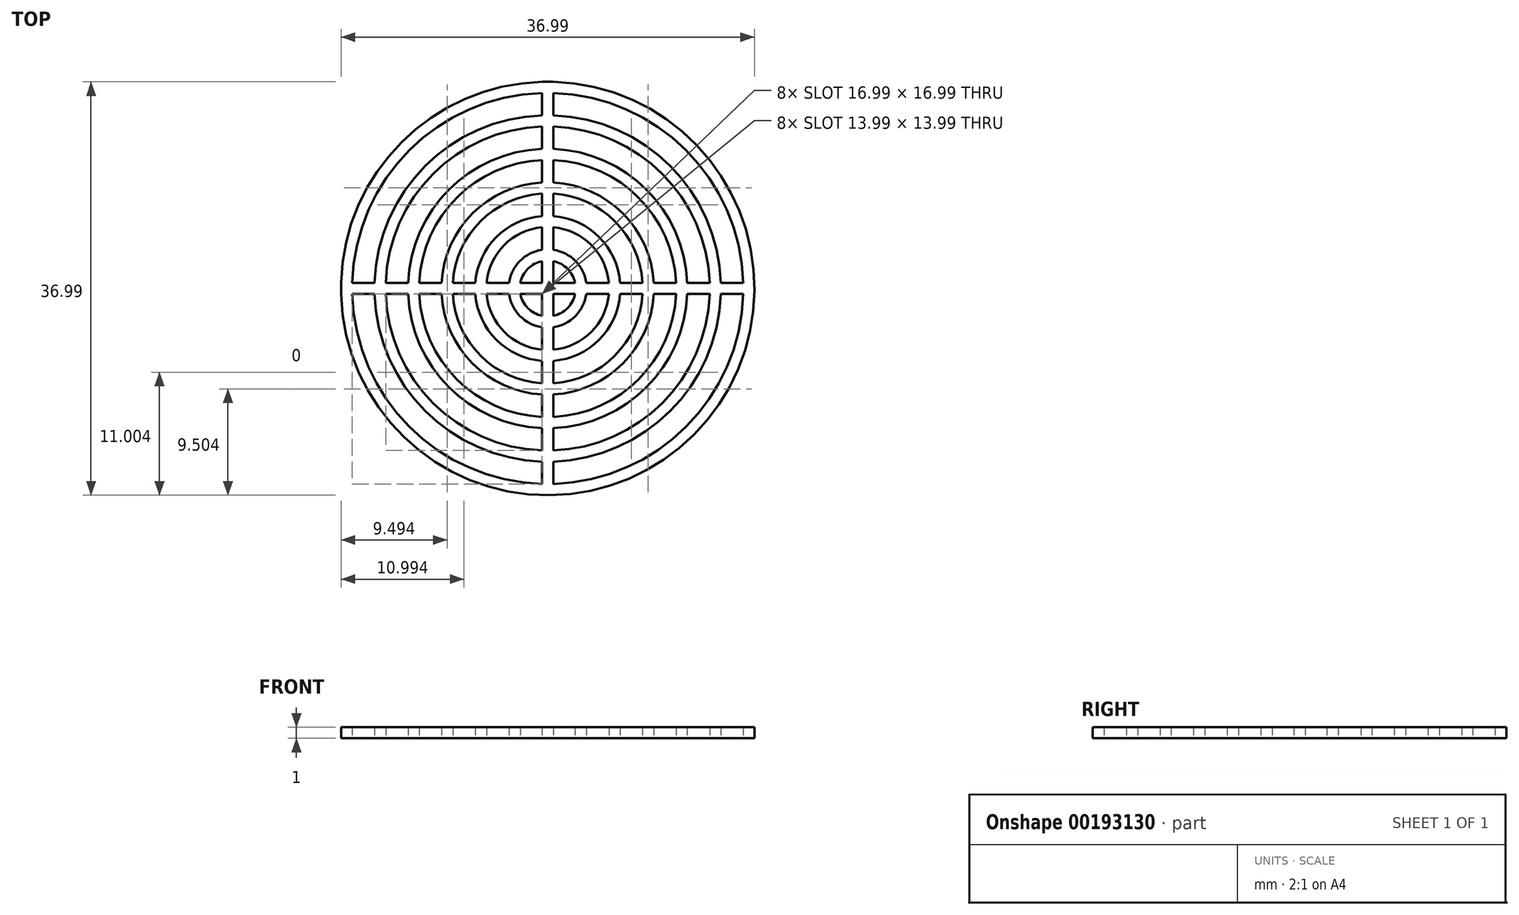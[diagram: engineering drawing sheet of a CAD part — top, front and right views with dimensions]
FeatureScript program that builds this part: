
annotation { "Feature Type Name" : "Feature", "Feature Type Description" : "" }
export const myFeature = defineFeature(function(context is Context, id is Id, definition is map)
    precondition{}
    {
        {
            var Q0;
            Q0=qCreatedBy(makeId("Top.planeOp"),FACE);
            var sketch = newSketch(context, id + "F0", { "sketchPlane" : qUnion([Q0])});
            skArc(sketch, "E0", {"start": v(-2.45, -0.5) * mm, "mid": v(-1.77, -1.77) * mm, "end": v(-0.5, -2.45) * mm});
            skArc(sketch, "E1", {"start": v(-3.46, -0.5) * mm, "mid": v(-2.47, -2.47) * mm, "end": v(-0.5, -3.46) * mm});
            skArc(sketch, "E2", {"start": v(-5.48, -0.5) * mm, "mid": v(-3.89, -3.89) * mm, "end": v(-0.5, -5.48) * mm});
            skArc(sketch, "E3", {"start": v(-6.48, -0.5) * mm, "mid": v(-4.6, -4.6) * mm, "end": v(-0.5, -6.48) * mm});
            skArc(sketch, "E4", {"start": v(-8.49, -0.5) * mm, "mid": v(-6.01, -6.01) * mm, "end": v(-0.5, -8.49) * mm});
            skArc(sketch, "E5", {"start": v(-9.49, -0.5) * mm, "mid": v(-6.72, -6.72) * mm, "end": v(-0.5, -9.49) * mm});
            skArc(sketch, "E6", {"start": v(-11.49, -0.5) * mm, "mid": v(-8.13, -8.13) * mm, "end": v(-0.5, -11.49) * mm});
            skArc(sketch, "E7", {"start": v(-12.49, -0.5) * mm, "mid": v(-8.84, -8.84) * mm, "end": v(-0.5, -12.49) * mm});
            skArc(sketch, "E8", {"start": v(-14.5, -0.5) * mm, "mid": v(-10.25, -10.25) * mm, "end": v(-0.5, -14.5) * mm});
            skArc(sketch, "E9", {"start": v(-15.5, -0.5) * mm, "mid": v(-10.96, -10.96) * mm, "end": v(-0.5, -15.5) * mm});
            skArc(sketch, "E10", {"start": v(-17.5, -0.5) * mm, "mid": v(-12.37, -12.37) * mm, "end": v(-0.5, -17.5) * mm});
            skArc(sketch, "E11", {"start": v(-18.5, -0.5) * mm, "mid": v(13.08, -13.08) * mm, "end": v(0.5, 18.5) * mm});
            skLineSegment(sketch, "E12", {"start": v(-17.5, 0.5) * mm, "end": v(-15.5, 0.5) * mm});
            skLineSegment(sketch, "E13", {"start": v(17.5, -0.5) * mm, "end": v(15.5, -0.5) * mm});
            skLineSegment(sketch, "E14", {"start": v(-18.5, -0.5) * mm, "end": v(-18.5, 0.5) * mm});
            skLineSegment(sketch, "E15", {"start": v(-0.5, -17.5) * mm, "end": v(-0.5, -15.5) * mm});
            skLineSegment(sketch, "E16", {"start": v(-0.5, 18.5) * mm, "end": v(0.5, 18.5) * mm});
            skLineSegment(sketch, "E17", {"start": v(0.5, 17.5) * mm, "end": v(0.5, 15.5) * mm});
            skLineSegment(sketch, "E18.trimOffspring", {"start": v(-14.5, 0.5) * mm, "end": v(-12.49, 0.5) * mm});
            skLineSegment(sketch, "E19.trimOffspring", {"start": v(-15.5, -0.5) * mm, "end": v(-17.5, -0.5) * mm});
            skLineSegment(sketch, "E20.trimOffspring", {"start": v(-11.49, 0.5) * mm, "end": v(-9.49, 0.5) * mm});
            skLineSegment(sketch, "E21.trimOffspring", {"start": v(-12.49, -0.5) * mm, "end": v(-14.5, -0.5) * mm});
            skLineSegment(sketch, "E22.trimOffspring", {"start": v(0.5, 0.5) * mm, "end": v(2.45, 0.5) * mm});
            skLineSegment(sketch, "E23.trimOffspring", {"start": v(-0.5, 0.5) * mm, "end": v(-0.5, 2.45) * mm});
            skLineSegment(sketch, "E24.trimOffspring", {"start": v(0.5, -0.5) * mm, "end": v(0.5, -2.45) * mm});
            skLineSegment(sketch, "E25.trimOffspring", {"start": v(-0.5, -0.5) * mm, "end": v(-2.45, -0.5) * mm});
            skArc(sketch, "E26.trimOffspring", {"start": v(2.45, 0.5) * mm, "mid": v(1.77, 1.77) * mm, "end": v(0.5, 2.45) * mm});
            skArc(sketch, "E27.trimOffspring", {"start": v(3.46, 0.5) * mm, "mid": v(2.47, 2.47) * mm, "end": v(0.5, 3.46) * mm});
            skArc(sketch, "E28.trimOffspring", {"start": v(5.48, 0.5) * mm, "mid": v(3.89, 3.89) * mm, "end": v(0.5, 5.48) * mm});
            skArc(sketch, "E29.trimOffspring", {"start": v(6.48, 0.5) * mm, "mid": v(4.6, 4.6) * mm, "end": v(0.5, 6.48) * mm});
            skArc(sketch, "E30.trimOffspring", {"start": v(8.49, 0.5) * mm, "mid": v(6.01, 6.01) * mm, "end": v(0.5, 8.49) * mm});
            skArc(sketch, "E31.trimOffspring", {"start": v(9.49, 0.5) * mm, "mid": v(6.72, 6.72) * mm, "end": v(0.5, 9.49) * mm});
            skArc(sketch, "E32.trimOffspring", {"start": v(12.49, 0.5) * mm, "mid": v(8.84, 8.84) * mm, "end": v(0.5, 12.49) * mm});
            skArc(sketch, "E33.trimOffspring", {"start": v(11.49, 0.5) * mm, "mid": v(8.13, 8.13) * mm, "end": v(0.5, 11.49) * mm});
            skArc(sketch, "E34.trimOffspring", {"start": v(14.5, 0.5) * mm, "mid": v(10.25, 10.25) * mm, "end": v(0.5, 14.5) * mm});
            skArc(sketch, "E35.trimOffspring", {"start": v(15.5, 0.5) * mm, "mid": v(10.96, 10.96) * mm, "end": v(0.5, 15.5) * mm});
            skArc(sketch, "E36.trimOffspring", {"start": v(17.5, 0.5) * mm, "mid": v(12.37, 12.37) * mm, "end": v(0.5, 17.5) * mm});
            skLineSegment(sketch, "E37.trimOffspring", {"start": v(14.5, -0.5) * mm, "end": v(12.49, -0.5) * mm});
            skLineSegment(sketch, "E38.trimOffspring", {"start": v(15.5, 0.5) * mm, "end": v(17.5, 0.5) * mm});
            skLineSegment(sketch, "E39.trimOffspring", {"start": v(12.49, 0.5) * mm, "end": v(14.5, 0.5) * mm});
            skLineSegment(sketch, "E40.trimOffspring", {"start": v(11.49, -0.5) * mm, "end": v(9.49, -0.5) * mm});
            skLineSegment(sketch, "E41.trimOffspring", {"start": v(8.49, -0.5) * mm, "end": v(6.48, -0.5) * mm});
            skLineSegment(sketch, "E42.trimOffspring", {"start": v(9.49, 0.5) * mm, "end": v(11.49, 0.5) * mm});
            skLineSegment(sketch, "E43.trimOffspring", {"start": v(6.48, 0.5) * mm, "end": v(8.49, 0.5) * mm});
            skLineSegment(sketch, "E44.trimOffspring", {"start": v(5.48, -0.5) * mm, "end": v(3.46, -0.5) * mm});
            skLineSegment(sketch, "E45.trimOffspring", {"start": v(2.45, -0.5) * mm, "end": v(0.5, -0.5) * mm});
            skLineSegment(sketch, "E46.trimOffspring", {"start": v(3.46, 0.5) * mm, "end": v(5.48, 0.5) * mm});
            skLineSegment(sketch, "E47.trimOffspring", {"start": v(-2.45, 0.5) * mm, "end": v(-0.5, 0.5) * mm});
            skLineSegment(sketch, "E48.trimOffspring", {"start": v(-3.46, -0.5) * mm, "end": v(-5.48, -0.5) * mm});
            skLineSegment(sketch, "E49.trimOffspring", {"start": v(-6.48, -0.5) * mm, "end": v(-8.49, -0.5) * mm});
            skLineSegment(sketch, "E50.trimOffspring", {"start": v(-5.48, 0.5) * mm, "end": v(-3.46, 0.5) * mm});
            skLineSegment(sketch, "E51.trimOffspring", {"start": v(-8.49, 0.5) * mm, "end": v(-6.48, 0.5) * mm});
            skLineSegment(sketch, "E52.trimOffspring", {"start": v(-9.49, -0.5) * mm, "end": v(-11.49, -0.5) * mm});
            skPoint(sketch, "E53.start.orphan", {"position": v(18.5, 0.5) * mm});
            skArc(sketch, "E54.trimOffspring", {"start": v(-0.5, 2.45) * mm, "mid": v(-1.77, 1.77) * mm, "end": v(-2.45, 0.5) * mm});
            skLineSegment(sketch, "E55.trimOffspring", {"start": v(-0.5, 3.46) * mm, "end": v(-0.5, 5.48) * mm});
            skLineSegment(sketch, "E56.trimOffspring", {"start": v(0.5, 2.45) * mm, "end": v(0.5, 0.5) * mm});
            skArc(sketch, "E57.trimOffspring", {"start": v(-0.5, 3.46) * mm, "mid": v(-2.47, 2.47) * mm, "end": v(-3.46, 0.5) * mm});
            skArc(sketch, "E58.trimOffspring", {"start": v(-0.5, 5.48) * mm, "mid": v(-3.89, 3.89) * mm, "end": v(-5.48, 0.5) * mm});
            skLineSegment(sketch, "E59.trimOffspring", {"start": v(-0.5, 6.48) * mm, "end": v(-0.5, 8.49) * mm});
            skArc(sketch, "E60.trimOffspring", {"start": v(-0.5, 6.48) * mm, "mid": v(-4.6, 4.6) * mm, "end": v(-6.48, 0.5) * mm});
            skLineSegment(sketch, "E61.trimOffspring", {"start": v(0.5, 5.48) * mm, "end": v(0.5, 3.46) * mm});
            skArc(sketch, "E62.trimOffspring", {"start": v(-0.5, 8.49) * mm, "mid": v(-6.01, 6.01) * mm, "end": v(-8.49, 0.5) * mm});
            skLineSegment(sketch, "E63.trimOffspring", {"start": v(-0.5, 9.49) * mm, "end": v(-0.5, 11.49) * mm});
            skArc(sketch, "E64.trimOffspring", {"start": v(-0.5, 9.49) * mm, "mid": v(-6.72, 6.72) * mm, "end": v(-9.49, 0.5) * mm});
            skLineSegment(sketch, "E65.trimOffspring", {"start": v(0.5, 8.49) * mm, "end": v(0.5, 6.48) * mm});
            skArc(sketch, "E66.trimOffspring", {"start": v(-0.5, 11.49) * mm, "mid": v(-8.13, 8.13) * mm, "end": v(-11.49, 0.5) * mm});
            skLineSegment(sketch, "E67.trimOffspring", {"start": v(-0.5, 12.49) * mm, "end": v(-0.5, 14.5) * mm});
            skArc(sketch, "E68.trimOffspring", {"start": v(-0.5, 12.49) * mm, "mid": v(-8.84, 8.84) * mm, "end": v(-12.49, 0.5) * mm});
            skLineSegment(sketch, "E69.trimOffspring", {"start": v(0.5, 11.49) * mm, "end": v(0.5, 9.49) * mm});
            skArc(sketch, "E70.trimOffspring", {"start": v(-0.5, 14.5) * mm, "mid": v(-10.25, 10.25) * mm, "end": v(-14.5, 0.5) * mm});
            skLineSegment(sketch, "E71.trimOffspring", {"start": v(-0.5, 15.5) * mm, "end": v(-0.5, 17.5) * mm});
            skArc(sketch, "E72.trimOffspring", {"start": v(-0.5, 15.5) * mm, "mid": v(-10.96, 10.96) * mm, "end": v(-15.5, 0.5) * mm});
            skLineSegment(sketch, "E73.trimOffspring", {"start": v(0.5, 14.5) * mm, "end": v(0.5, 12.49) * mm});
            skArc(sketch, "E74.trimOffspring", {"start": v(-0.5, 17.5) * mm, "mid": v(-12.37, 12.37) * mm, "end": v(-17.5, 0.5) * mm});
            skArc(sketch, "E75.trimOffspring", {"start": v(-0.5, 18.5) * mm, "mid": v(-13.08, 13.08) * mm, "end": v(-18.5, 0.5) * mm});
            skArc(sketch, "E76.trimOffspring", {"start": v(0.5, -2.45) * mm, "mid": v(1.77, -1.77) * mm, "end": v(2.45, -0.5) * mm});
            skLineSegment(sketch, "E77.trimOffspring", {"start": v(-0.5, -2.45) * mm, "end": v(-0.5, -0.5) * mm});
            skLineSegment(sketch, "E78.trimOffspring", {"start": v(0.5, -3.46) * mm, "end": v(0.5, -5.48) * mm});
            skArc(sketch, "E79.trimOffspring", {"start": v(0.5, -3.46) * mm, "mid": v(2.47, -2.47) * mm, "end": v(3.46, -0.5) * mm});
            skArc(sketch, "E80.trimOffspring", {"start": v(0.5, -5.48) * mm, "mid": v(3.89, -3.89) * mm, "end": v(5.48, -0.5) * mm});
            skLineSegment(sketch, "E81.trimOffspring", {"start": v(-0.5, -5.48) * mm, "end": v(-0.5, -3.46) * mm});
            skArc(sketch, "E82.trimOffspring", {"start": v(0.5, -6.48) * mm, "mid": v(4.6, -4.6) * mm, "end": v(6.48, -0.5) * mm});
            skLineSegment(sketch, "E83.trimOffspring", {"start": v(0.5, -6.48) * mm, "end": v(0.5, -8.49) * mm});
            skLineSegment(sketch, "E84.trimOffspring", {"start": v(-0.5, -8.49) * mm, "end": v(-0.5, -6.48) * mm});
            skLineSegment(sketch, "E85.trimOffspring", {"start": v(0.5, -9.49) * mm, "end": v(0.5, -11.49) * mm});
            skArc(sketch, "E86.trimOffspring", {"start": v(0.5, -9.49) * mm, "mid": v(6.72, -6.72) * mm, "end": v(9.49, -0.5) * mm});
            skArc(sketch, "E87.trimOffspring", {"start": v(0.5, -8.49) * mm, "mid": v(6.01, -6.01) * mm, "end": v(8.49, -0.5) * mm});
            skArc(sketch, "E88.trimOffspring", {"start": v(0.5, -11.49) * mm, "mid": v(8.13, -8.13) * mm, "end": v(11.49, -0.5) * mm});
            skLineSegment(sketch, "E89.trimOffspring", {"start": v(-0.5, -11.49) * mm, "end": v(-0.5, -9.49) * mm});
            skArc(sketch, "E90.trimOffspring", {"start": v(0.5, -12.49) * mm, "mid": v(8.84, -8.84) * mm, "end": v(12.49, -0.5) * mm});
            skArc(sketch, "E91.trimOffspring", {"start": v(0.5, -14.5) * mm, "mid": v(10.25, -10.25) * mm, "end": v(14.5, -0.5) * mm});
            skArc(sketch, "E92.trimOffspring", {"start": v(0.5, -15.5) * mm, "mid": v(10.96, -10.96) * mm, "end": v(15.5, -0.5) * mm});
            skArc(sketch, "E93.trimOffspring", {"start": v(0.5, -17.5) * mm, "mid": v(12.37, -12.37) * mm, "end": v(17.5, -0.5) * mm});
            skLineSegment(sketch, "E94.trimOffspring", {"start": v(0.5, -12.49) * mm, "end": v(0.5, -14.5) * mm});
            skLineSegment(sketch, "E95.trimOffspring", {"start": v(0.5, -15.5) * mm, "end": v(0.5, -17.5) * mm});
            skLineSegment(sketch, "E96.trimOffspring", {"start": v(-0.5, -14.5) * mm, "end": v(-0.5, -12.49) * mm});
            skSolve(sketch);
        }
        {
            var Q0;
            Q0=makeQuery(id+"F0.imprint","IMPRINT",FACE,{"disambiguationData":[TD([[makeQuery(id+"F0.imprint","IMPRINT",EDGE,{"derivedFrom":sQuery(id+"F0.wireOp",EDGE,"E0")}),-1.0]])]});
            extrude(context, id + "F1", {"entities" : qUnion([Q0]), "depth" : 1 * mm});
        }
    });
